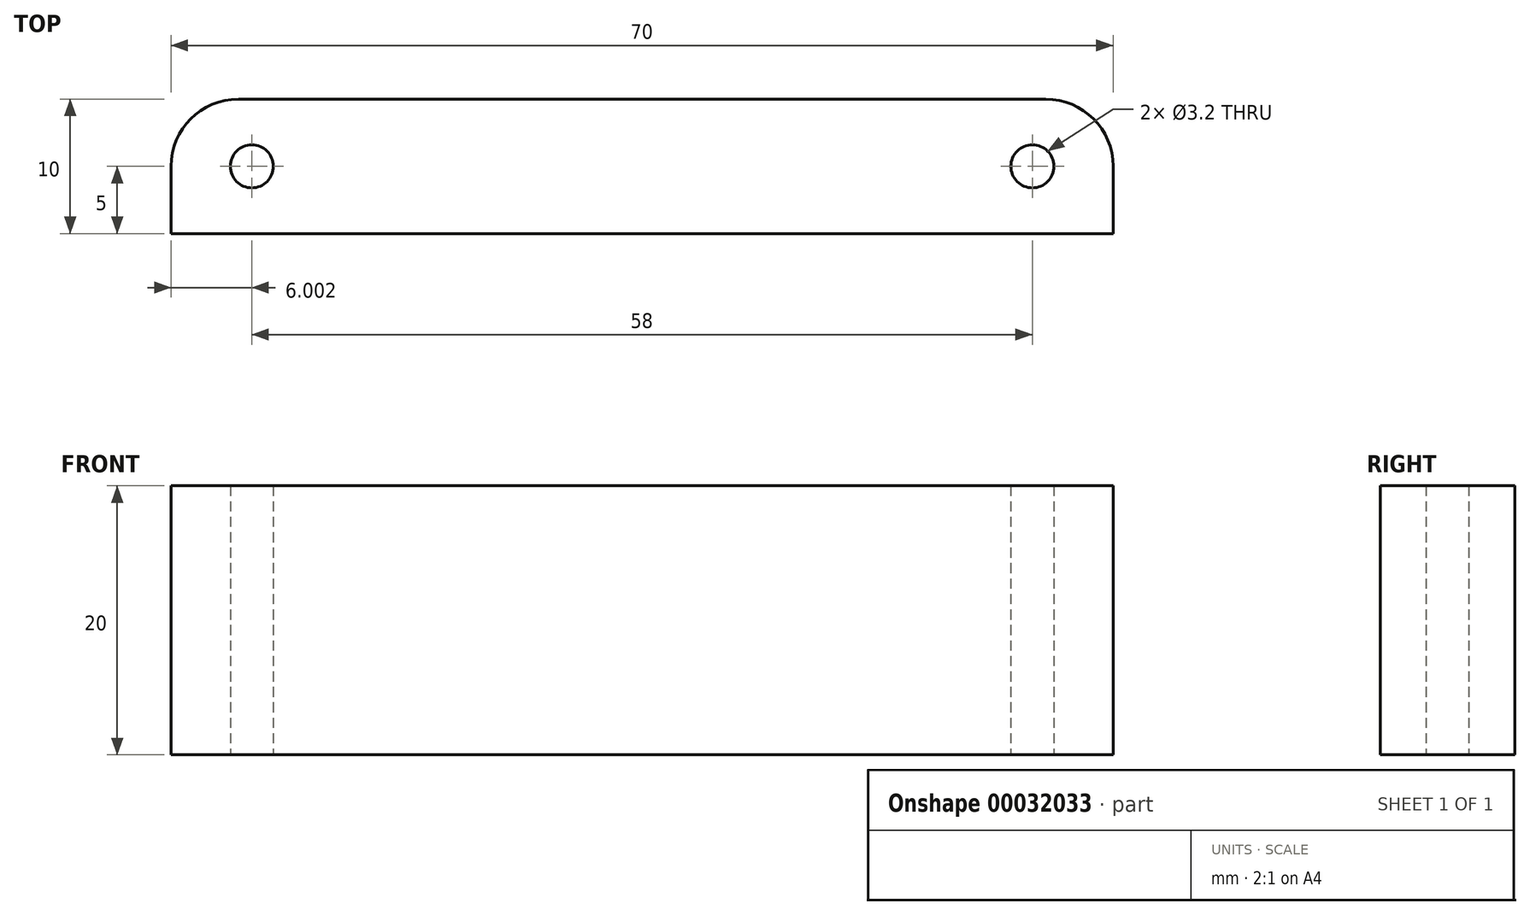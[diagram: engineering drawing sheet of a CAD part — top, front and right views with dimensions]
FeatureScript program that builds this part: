
annotation { "Feature Type Name" : "Feature", "Feature Type Description" : "" }
export const myFeature = defineFeature(function(context is Context, id is Id, definition is map)
    precondition{}
    {
        {
            var Q0;
            Q0=qCreatedBy(makeId("Top.planeOp"),FACE);
            var sketch = newSketch(context, id + "F0", { "sketchPlane" : qUnion([Q0])});
            skCircle(sketch, "E0", {"center": v(-33.28, 0) * mm, "radius": 1.6 * mm});
            skCircle(sketch, "E1", {"center": v(24.72, 0) * mm, "radius": 1.6 * mm});
            skLineSegment(sketch, "E2.bottom", {"start": v(-33.28, 5) * mm, "end": v(24.72, 5) * mm});
            skLineSegment(sketch, "E2.top", {"start": v(-33.28, -5) * mm, "end": v(24.72, -5) * mm});
            skLineSegment(sketch, "E2.left", {"start": v(-33.28, 5) * mm, "end": v(-33.28, -5) * mm, "construction": true});
            skLineSegment(sketch, "E2.right", {"start": v(24.72, 5) * mm, "end": v(24.72, -5) * mm, "construction": true});
            skLineSegment(sketch, "E3.bottom", {"start": v(-33.28, 5) * mm, "end": v(-39.28, 5) * mm});
            skLineSegment(sketch, "E3.top", {"start": v(-33.28, -5) * mm, "end": v(-39.28, -5) * mm});
            skLineSegment(sketch, "E3.right", {"start": v(-39.28, 5) * mm, "end": v(-39.28, -5) * mm});
            skLineSegment(sketch, "E4.bottom", {"start": v(24.72, 5) * mm, "end": v(30.72, 5) * mm});
            skLineSegment(sketch, "E4.top", {"start": v(24.72, -5) * mm, "end": v(30.72, -5) * mm});
            skLineSegment(sketch, "E4.right", {"start": v(30.72, 5) * mm, "end": v(30.72, -5) * mm});
            skSolve(sketch);
        }
        {
            var Q0;
            Q0 = qSketchRegion(id + "F0", true);
            extrude(context, id + "F1", {"entities" : qUnion([Q0]), "depth" : 20 * mm});
        }
        {
            var Q0;
            Q0=makeQuery(id+"F1.opExtrude","SWEPT_EDGE",EDGE,{"disambiguationData":[OSD([sQuery(id+"F0.wireOp",EDGE,"E3.bottom"),sQuery(id+"F0.wireOp",EDGE,"E3.right")])]});
            var Q1;
            Q1=makeQuery(id+"F1.opExtrude","SWEPT_EDGE",EDGE,{"disambiguationData":[OSD([sQuery(id+"F0.wireOp",EDGE,"E4.bottom"),sQuery(id+"F0.wireOp",EDGE,"E4.right")])]});
            fillet(context, id + "F2", {"entities" : qUnion([Q0, Q1]), "radius" : 5 * mm, "tangentPropagation" : true, "allowEdgeOverflow" : false});
        }
    });
